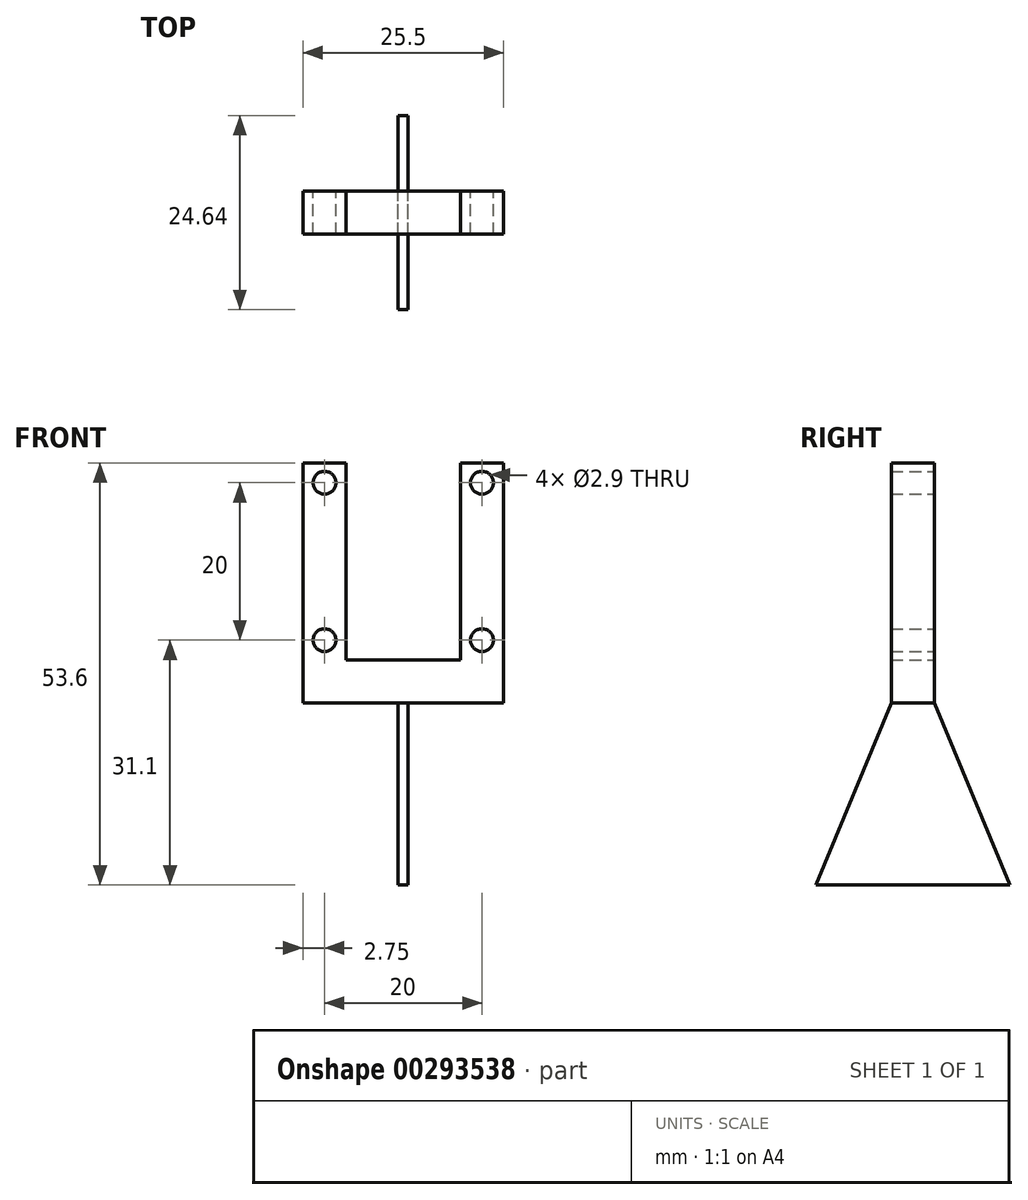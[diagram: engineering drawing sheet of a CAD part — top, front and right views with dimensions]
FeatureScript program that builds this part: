
annotation { "Feature Type Name" : "Feature", "Feature Type Description" : "" }
export const myFeature = defineFeature(function(context is Context, id is Id, definition is map)
    precondition{}
    {
        {
            var Q0;
            Q0=qCreatedBy(makeId("Front.planeOp"),FACE);
            var sketch = newSketch(context, id + "F0", { "sketchPlane" : qUnion([Q0])});
            skLineSegment(sketch, "E0.bottom", {"start": v(12.75, 0) * mm, "end": v(7.25, 0) * mm});
            skLineSegment(sketch, "E0.top", {"start": v(12.75, 25) * mm, "end": v(7.25, 25) * mm});
            skLineSegment(sketch, "E0.left", {"start": v(12.75, 0) * mm, "end": v(12.75, 25) * mm});
            skLineSegment(sketch, "E0.right", {"start": v(7.25, 0) * mm, "end": v(7.25, 25) * mm});
            skCircle(sketch, "E1", {"center": v(10, 2.5) * mm, "radius": 1.45 * mm});
            skCircle(sketch, "E2", {"center": v(10, 22.5) * mm, "radius": 1.45 * mm});
            skLineSegment(sketch, "E3.MirrorCS", {"start": v(-12.75, 0) * mm, "end": v(-7.25, 0) * mm});
            skLineSegment(sketch, "E4.MirrorCS", {"start": v(-12.75, 25) * mm, "end": v(-7.25, 25) * mm});
            skLineSegment(sketch, "E5.MirrorCS", {"start": v(-12.75, 0) * mm, "end": v(-12.75, 25) * mm});
            skLineSegment(sketch, "E6.MirrorCS", {"start": v(-7.25, 0) * mm, "end": v(-7.25, 25) * mm});
            skCircle(sketch, "E7.MirrorC", {"center": v(-10, 2.5) * mm, "radius": 1.45 * mm});
            skCircle(sketch, "E8.MirrorC", {"center": v(-10, 22.5) * mm, "radius": 1.45 * mm});
            skLineSegment(sketch, "E9.bottom", {"start": v(-12.75, 0) * mm, "end": v(12.75, 0) * mm});
            skLineSegment(sketch, "E9.top", {"start": v(-12.75, -5.5) * mm, "end": v(12.75, -5.5) * mm});
            skLineSegment(sketch, "E9.left", {"start": v(-12.75, 0) * mm, "end": v(-12.75, -5.5) * mm});
            skLineSegment(sketch, "E9.right", {"start": v(12.75, 0) * mm, "end": v(12.75, -5.5) * mm});
            skSolve(sketch);
        }
        {
            var Q0;
            Q0=makeQuery(id+"F0.imprint","IMPRINT",FACE,{"disambiguationData":[TD([[makeQuery(id+"F0.imprint","IMPRINT",EDGE,{"derivedFrom":sQuery(id+"F0.wireOp",EDGE,"E4.MirrorCS")}),-1.0]])]});
            var Q1;
            Q1=makeQuery(id+"F0.imprint","IMPRINT",FACE,{"disambiguationData":[TD([[makeQuery(id+"F0.imprint","IMPRINT",EDGE,{"derivedFrom":sQuery(id+"F0.wireOp",EDGE,"E0.top")}),1.0]])]});
            var Q2;
            Q2=makeQuery(id+"F0.imprint","IMPRINT",FACE,{"disambiguationData":[TD([[makeQuery(id+"F0.imprint","IMPRINT",EDGE,{"derivedFrom":sQuery(id+"F0.wireOp",EDGE,"E9.top")}),1.0]])]});
            extrude(context, id + "F1", {"entities" : qUnion([Q0, Q1, Q2]), "depth" : 5.5 * mm});
        }
        {
            var Q0;
            Q0=qCreatedBy(makeId("Right.planeOp"),FACE);
            var sketch = newSketch(context, id + "F2", { "sketchPlane" : qUnion([Q0])});
            skLineSegment(sketch, "E10.0", {"start": v(-5.5, -5.5) * mm, "end": v(0, -5.5) * mm});
            skLineSegment(sketch, "E11", {"start": v(-5.5, -5.5) * mm, "end": v(-15.07, -28.6) * mm});
            skLineSegment(sketch, "E12", {"start": v(-2.75, -5.5) * mm, "end": v(-2.75, -18.45) * mm, "construction": true});
            skLineSegment(sketch, "E13.MirrorCS", {"start": v(0, -5.5) * mm, "end": v(9.57, -28.6) * mm});
            skLineSegment(sketch, "E14", {"start": v(-15.07, -28.6) * mm, "end": v(9.57, -28.6) * mm});
            skSolve(sketch);
        }
        {
            var Q0;
            Q0 = qSketchRegion(id + "F2", true);
            extrude(context, id + "F3", {"entities" : qUnion([Q0]), "operationType" : NewBodyOperationType.ADD, "endBound" : BoundingType.SYMMETRIC, "oppositeDirection" : true, "depth" : 1.27 * mm});
        }
    });
